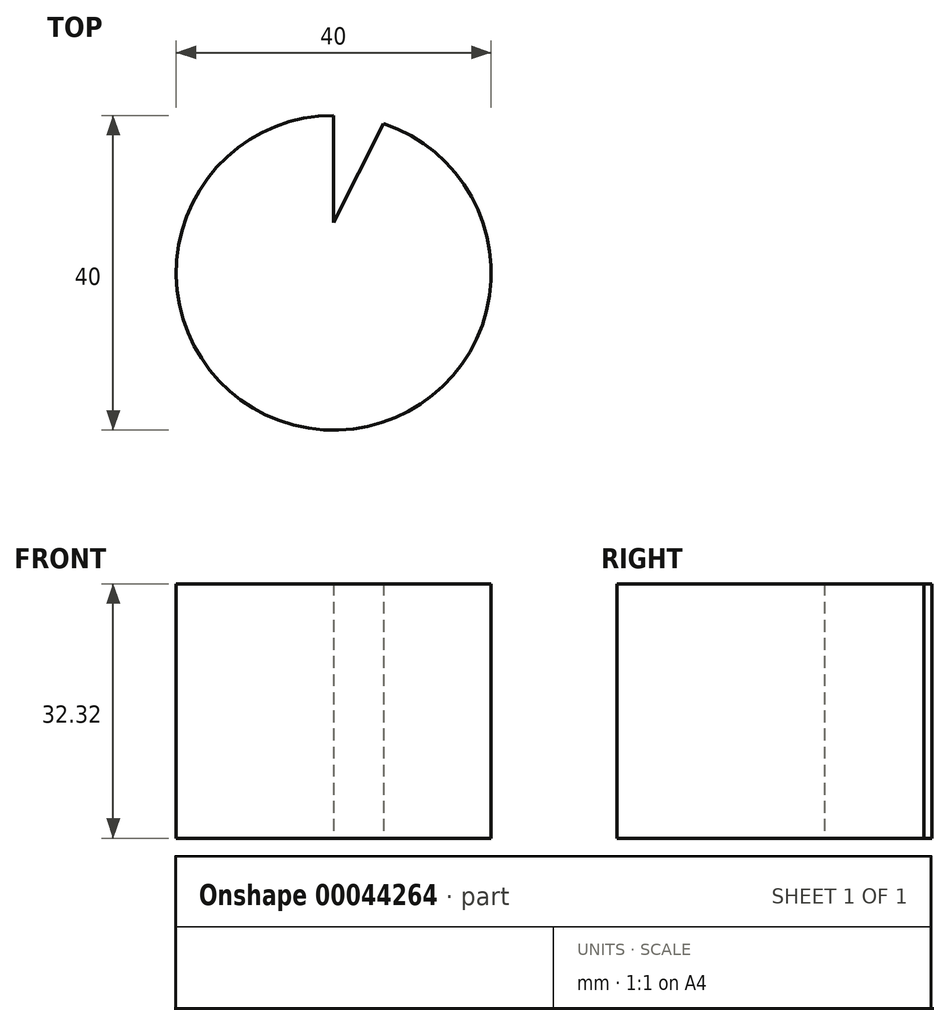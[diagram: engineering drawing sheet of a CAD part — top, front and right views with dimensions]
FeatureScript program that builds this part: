
annotation { "Feature Type Name" : "Feature", "Feature Type Description" : "" }
export const myFeature = defineFeature(function(context is Context, id is Id, definition is map)
    precondition{}
    {
        {
            var Q0;
            Q0=qCreatedBy(makeId("Top.planeOp"),FACE);
            var sketch = newSketch(context, id + "F0", { "sketchPlane" : qUnion([Q0])});
            skArc(sketch, "E0", {"start": v(0, 20) * mm, "mid": v(-3.2, -19.74) * mm, "end": v(6.3, 18.98) * mm});
            skLineSegment(sketch, "E1", {"start": v(0, 20) * mm, "end": v(0, 6.36) * mm});
            skLineSegment(sketch, "E2", {"start": v(0, 6.36) * mm, "end": v(6.3, 18.98) * mm});
            skSolve(sketch);
        }
        {
            var Q0;
            Q0 = qSketchRegion(id + "F0", true);
            extrude(context, id + "F1", {"entities" : qUnion([Q0]), "depth" : 25 * mm});
        }
        {
            var Q0;
            Q0=makeQuery(id+"F1.opExtrude","CAP_FACE",FACE,{"disambiguationData":[OSD([sQuery(id+"F0.wireOp",EDGE,"E0"),sQuery(id+"F0.wireOp",EDGE,"E1"),sQuery(id+"F0.wireOp",EDGE,"E2")])],"isStart":false});
            extrude(context, id + "F2", {"entities" : qUnion([Q0]), "operationType" : NewBodyOperationType.ADD, "depth" : 7.32 * mm});
        }
    });
